# Revit family: Seating-Teknion-CQSCH_Workshop_Stool-R2020
name_source: partatom
category: Furniture
units: mm (PartAtom-declared; Revit-internal decimal feet)

## family parameters
Always vertical = Yes
Cut with Voids When Loaded = No
OmniClass Number = 23.40.20.00
OmniClass Title = General Furniture and Specialties
Room Calculation Point = No
Shared = Yes
Work Plane-Based = No

## types (2) — shared parameters
Assembly Code = E2020200
Caster Finish = Plastic - Teknion - E - Ebony
Manufacturer = Teknion
Manufacturer Fax = 416.661.4586
Part Number = CQSCH
Product Documentation Link = https://assets.teknion.com
Product Line = Multi Use Seating
Product Page URL = https://www.teknion.com
Series = Routes
Sustainability Data = https://www.teknion.com
URL = www.teknion.com
Unit Weight URL = http://www.teknion.com
Warranty = http://www.teknion.com
zero-valued in all types: Default Elevation

## per-type parameters (varying)
| type | Back | Description | Model | No Back |
| No Back | No | Workshop Stool with no back | CQSCHN | Yes |
| With back | Yes | Workshop Stool with back | CQSCHW | No |

## geometry (parser evidence)
native form markers: Sweep x7
no freeform markers — native parametric forms only
